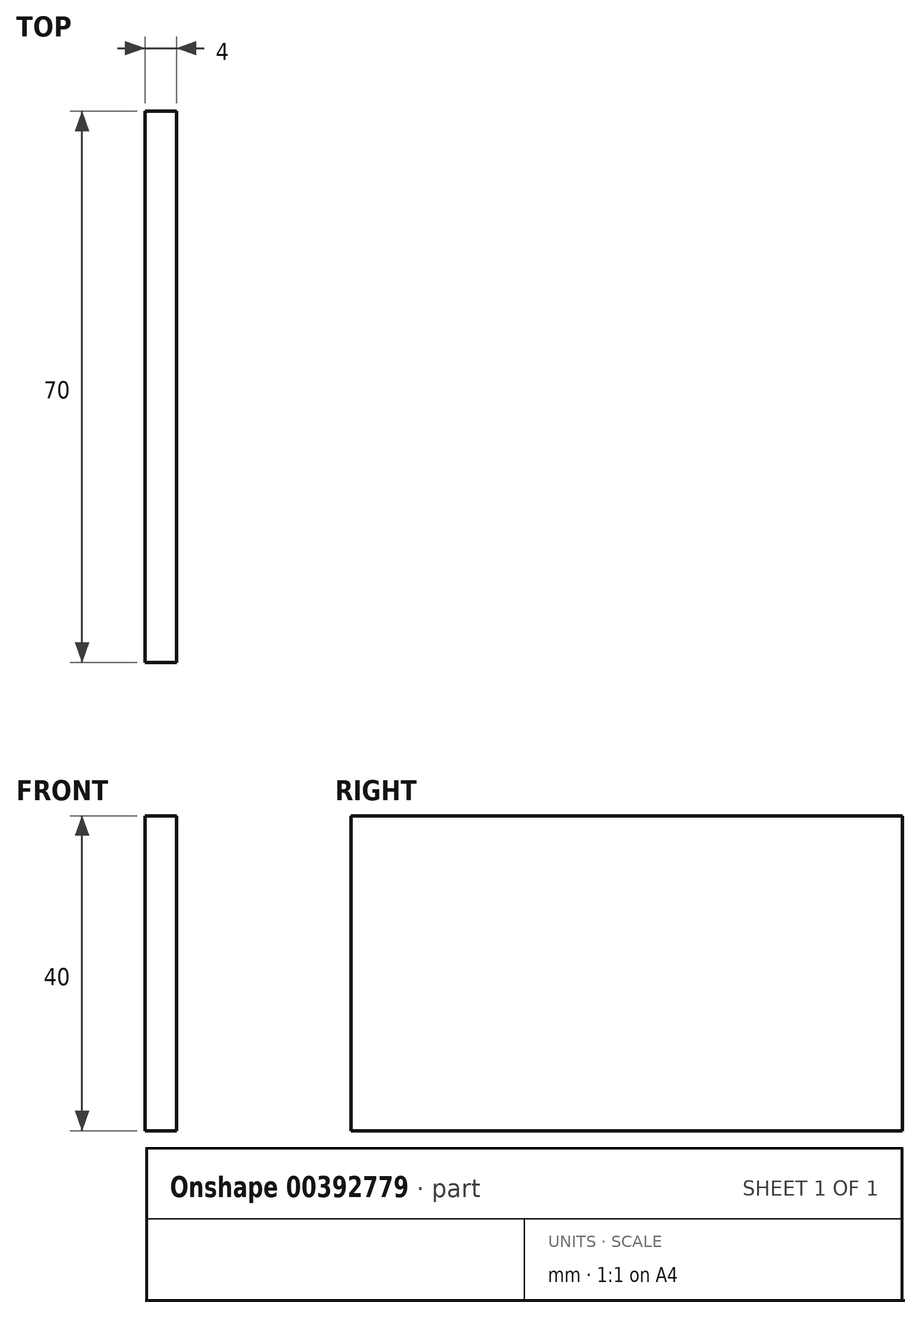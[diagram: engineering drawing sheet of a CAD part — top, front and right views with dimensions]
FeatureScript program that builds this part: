
annotation { "Feature Type Name" : "Feature", "Feature Type Description" : "" }
export const myFeature = defineFeature(function(context is Context, id is Id, definition is map)
    precondition{}
    {
        {
            var Q0;
            Q0=qCreatedBy(makeId("Top.planeOp"),FACE);
            var sketch = newSketch(context, id + "F0", { "sketchPlane" : qUnion([Q0])});
            skLineSegment(sketch, "E0.bottom", {"start": v(0, 0) * mm, "end": v(4, 0) * mm});
            skLineSegment(sketch, "E0.top", {"start": v(0, 70) * mm, "end": v(4, 70) * mm});
            skLineSegment(sketch, "E0.left", {"start": v(0, 0) * mm, "end": v(0, 70) * mm});
            skLineSegment(sketch, "E0.right", {"start": v(4, 0) * mm, "end": v(4, 70) * mm});
            skSolve(sketch);
        }
        {
            var Q0;
            Q0 = qSketchRegion(id + "F0", true);
            extrude(context, id + "F1", {"entities" : qUnion([Q0]), "depth" : 40 * mm});
        }
    });
